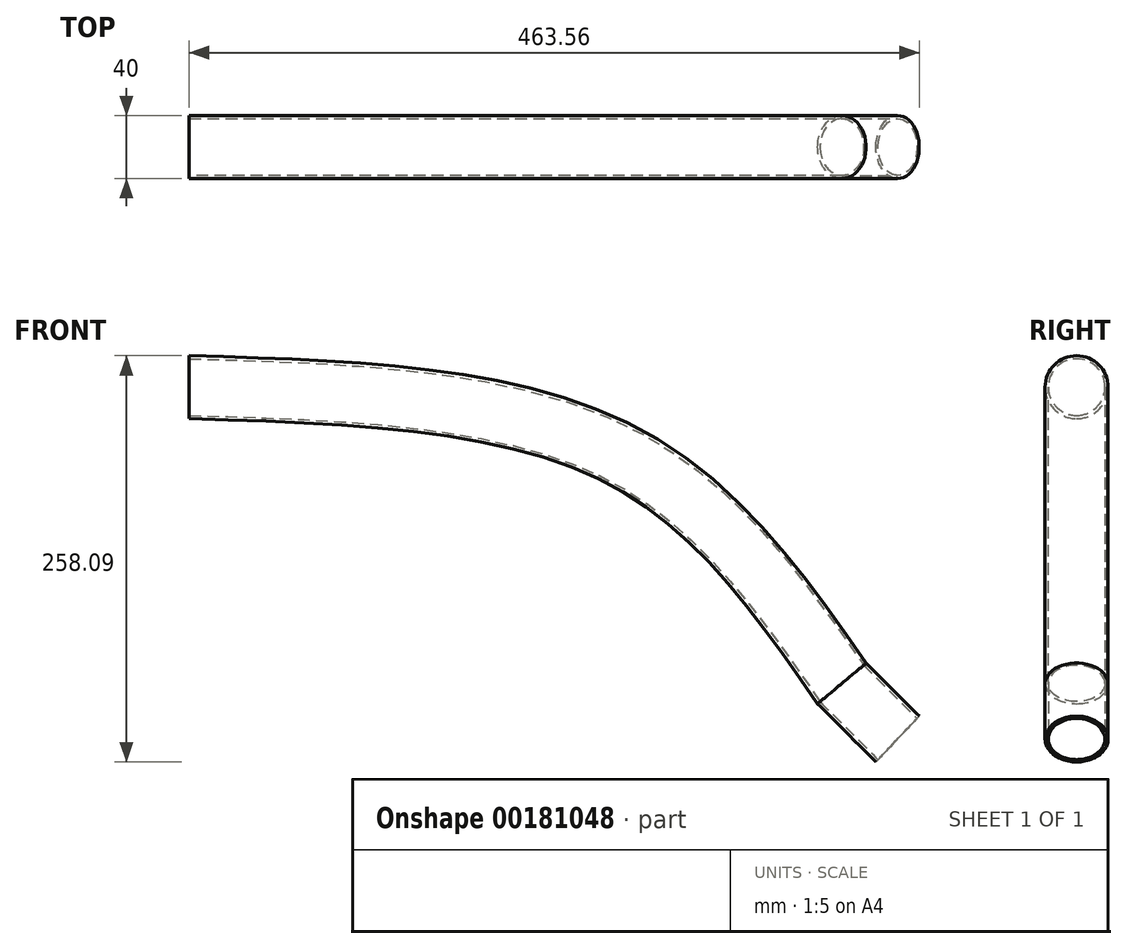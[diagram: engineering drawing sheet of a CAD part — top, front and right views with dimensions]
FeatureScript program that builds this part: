
annotation { "Feature Type Name" : "Feature", "Feature Type Description" : "" }
export const myFeature = defineFeature(function(context is Context, id is Id, definition is map)
    precondition{}
    {
        {
            var Q0;
            Q0=qCreatedBy(makeId("Front.planeOp"),FACE);
            var sketch = newSketch(context, id + "F0", { "sketchPlane" : qUnion([Q0])});
            skPoint(sketch, "E0", {"position": v(-243.64, 43.24) * mm});
            skPoint(sketch, "E1", {"position": v(206.2, 43.24) * mm});
            skPoint(sketch, "E2", {"position": v(206.2, -180.3) * mm});
            skLineSegment(sketch, "E3", {"start": v(206.2, -180.3) * mm, "end": v(170.84, -144.95) * mm});
            skFitSpline(sketch, "E4", {"points": [v(-243.64, 43.24) * mm, v(31.04, 0) * mm, v(170.84, -144.95) * mm], "startDerivative": vector(563.65, -16.49) * mm, "endDerivative": vector(257.1, -369.35) * mm});
            skSolve(sketch);
        }
        {
            var Q0;
            Q0=sQuery(id+"F0.wireOp",VERTEX,"E0");
            var Q1;
            Q1=qCreatedBy(makeId("Right.planeOp"),FACE);
            cPlane(context, id + "F1", {"entities" : qUnion([Q0, Q1]), "cplaneType" : CPlaneType.PLANE_POINT, "offset" : 25 * mm, "width" : 150 * mm, "height" : 150 * mm});
        }
        {
            var Q0;
            Q0=qCreatedBy(id+"F1.planeOp",FACE);
            var sketch = newSketch(context, id + "F2", { "sketchPlane" : qUnion([Q0])});
            skPoint(sketch, "E5.0", {"position": v(0, 43.24) * mm});
            skCircle(sketch, "E6", {"center": v(0, 43.24) * mm, "radius": 20 * mm});
            skCircle(sketch, "E7.0", {"center": v(0, 43.24) * mm, "radius": 18 * mm});
            skSolve(sketch);
        }
        {
            var Q0;
            Q0=makeQuery(id+"F2.imprint","IMPRINT",FACE,{"disambiguationData":[TD([[makeQuery(id+"F2.imprint","IMPRINT",EDGE,{"derivedFrom":sQuery(id+"F2.wireOp",EDGE,"E6")}),1.0]])]});
            var Q1;
            Q1=sQuery(id+"F0.wireOp",EDGE,"E4");
            var Q2;
            Q2=sQuery(id+"F0.wireOp",EDGE,"E3");
            sweep(context, id + "F3", {"profiles" : qUnion([Q0]), "path" : qUnion([Q1, Q2])});
        }
    });
